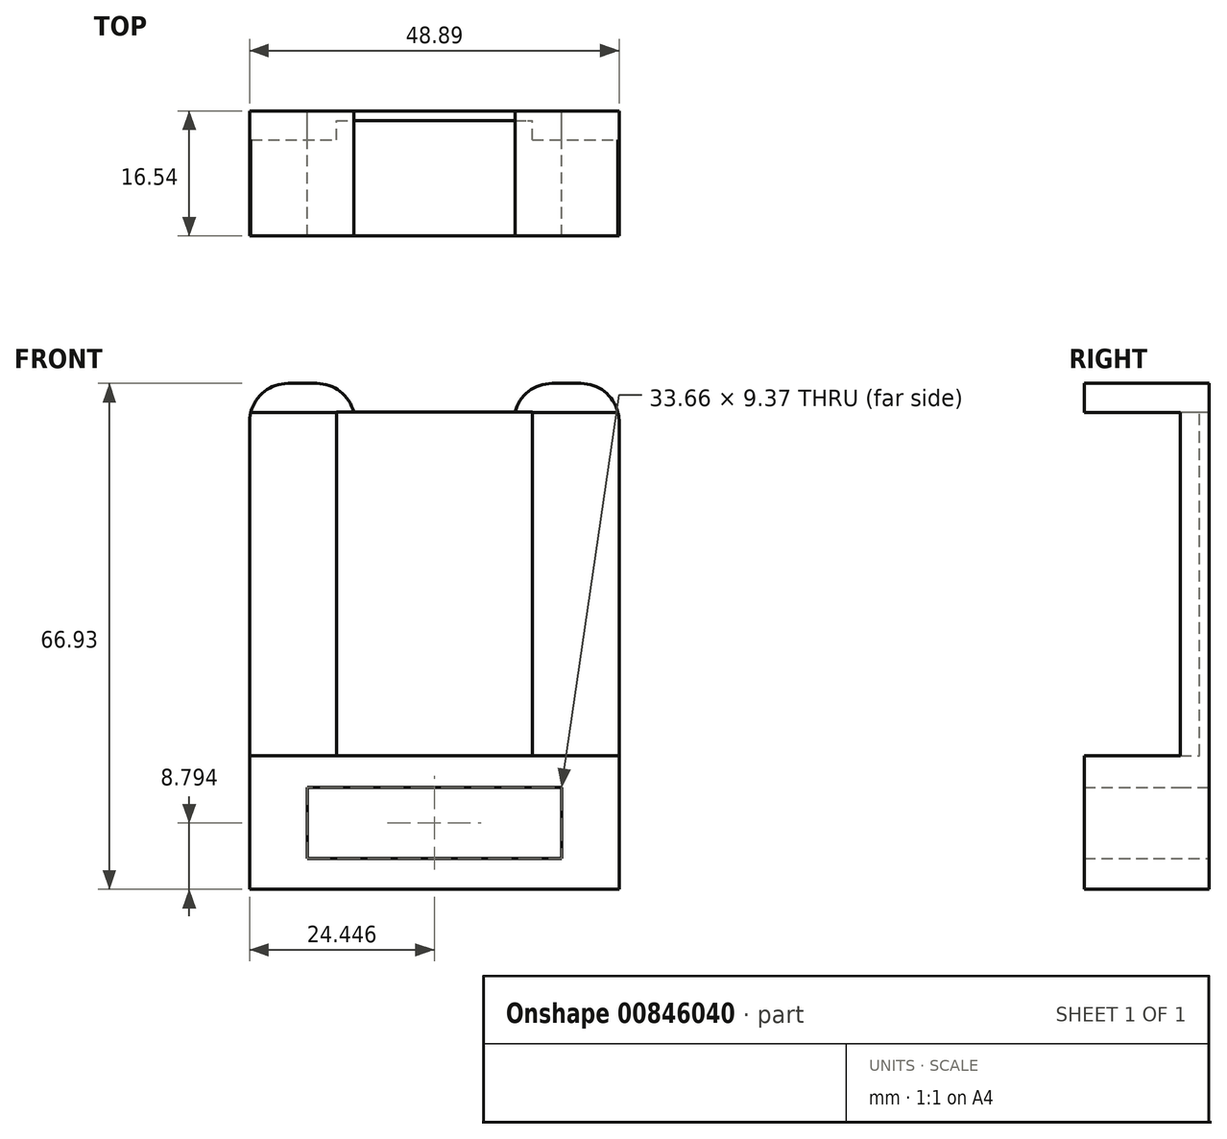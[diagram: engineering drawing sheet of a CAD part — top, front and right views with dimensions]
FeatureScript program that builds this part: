
annotation { "Feature Type Name" : "Feature", "Feature Type Description" : "" }
export const myFeature = defineFeature(function(context is Context, id is Id, definition is map)
    precondition{}
    {
        {
            var Q0;
            Q0=qCreatedBy(makeId("Front.planeOp"),FACE);
            var sketch = newSketch(context, id + "F0", { "sketchPlane" : qUnion([Q0])});
            skLineSegment(sketch, "E0.bottom", {"start": v(-13.58, -13.59) * mm, "end": v(20.07, -13.59) * mm});
            skLineSegment(sketch, "E0.top", {"start": v(-13.58, -4.22) * mm, "end": v(20.07, -4.22) * mm});
            skLineSegment(sketch, "E0.left", {"start": v(-13.58, -13.59) * mm, "end": v(-13.58, -4.22) * mm});
            skLineSegment(sketch, "E0.right", {"start": v(20.07, -13.59) * mm, "end": v(20.07, -4.22) * mm});
            skLineSegment(sketch, "E1.bottom", {"start": v(-21.2, -17.7) * mm, "end": v(27.7, -17.7) * mm});
            skLineSegment(sketch, "E1.left", {"start": v(-21.2, -17.7) * mm, "end": v(-21.2, 0) * mm});
            skLineSegment(sketch, "E1.right", {"start": v(27.7, -17.7) * mm, "end": v(27.7, 0) * mm});
            skLineSegment(sketch, "E2.bottom", {"start": v(-21.2, 0) * mm, "end": v(-9.7, 0) * mm});
            skLineSegment(sketch, "E2.top", {"start": v(-21.2, 45.42) * mm, "end": v(-9.7, 45.42) * mm});
            skLineSegment(sketch, "E2.left", {"start": v(-21.2, 0) * mm, "end": v(-21.2, 45.42) * mm});
            skLineSegment(sketch, "E2.right", {"start": v(-9.7, 0) * mm, "end": v(-9.7, 45.42) * mm});
            skPoint(sketch, "E3", {"position": v(3.25, 0) * mm});
            skLineSegment(sketch, "E4", {"start": v(3.25, 0) * mm, "end": v(3.25, 45.26) * mm, "construction": true});
            skLineSegment(sketch, "E5.MirrorCS", {"start": v(27.7, 45.42) * mm, "end": v(16.2, 45.42) * mm});
            skLineSegment(sketch, "E6.MirrorCS", {"start": v(27.7, 0) * mm, "end": v(27.7, 45.42) * mm});
            skLineSegment(sketch, "E7.MirrorCS", {"start": v(16.2, 0) * mm, "end": v(16.2, 45.42) * mm});
            skLineSegment(sketch, "E8", {"start": v(-9.7, 0) * mm, "end": v(-9.7, -4.22) * mm});
            skLineSegment(sketch, "E9", {"start": v(16.2, 0) * mm, "end": v(16.2, -4.22) * mm});
            skLineSegment(sketch, "E10", {"start": v(-9.7, 0) * mm, "end": v(16.2, 0) * mm});
            skLineSegment(sketch, "E11", {"start": v(16.2, 0) * mm, "end": v(27.7, 0) * mm});
            skLineSegment(sketch, "E12", {"start": v(-9.7, 45.42) * mm, "end": v(16.2, 45.42) * mm});
            skLineSegment(sketch, "E13.bottom", {"start": v(27.7, 45.42) * mm, "end": v(13.9, 45.42) * mm});
            skLineSegment(sketch, "E13.top", {"start": v(27.7, 49.23) * mm, "end": v(13.9, 49.23) * mm});
            skLineSegment(sketch, "E13.left", {"start": v(27.7, 45.42) * mm, "end": v(27.7, 49.23) * mm});
            skLineSegment(sketch, "E13.right", {"start": v(13.9, 45.42) * mm, "end": v(13.9, 49.23) * mm});
            skLineSegment(sketch, "E14.bottom", {"start": v(-21.2, 45.42) * mm, "end": v(-7.4, 45.42) * mm});
            skLineSegment(sketch, "E14.top", {"start": v(-21.2, 49.23) * mm, "end": v(-7.4, 49.23) * mm});
            skLineSegment(sketch, "E14.left", {"start": v(-21.2, 45.42) * mm, "end": v(-21.2, 49.23) * mm});
            skLineSegment(sketch, "E14.right", {"start": v(-7.4, 45.42) * mm, "end": v(-7.4, 49.23) * mm});
            skSolve(sketch);
        }
        {
            var Q0;
            Q0=makeQuery(id+"F0.imprint","IMPRINT",FACE,{"disambiguationData":[TD([[makeQuery(id+"F0.imprint","IMPRINT",EDGE,{"derivedFrom":sQuery(id+"F0.wireOp",EDGE,"E0.bottom")}),-1.0]])]});
            var Q1;
            {var subQ0=sQuery(id+"F0.wireOp",EDGE,"E6.MirrorCS");Q1=makeQuery(id+"F0.imprint","IMPRINT",FACE,{"disambiguationData":[TD([[makeQuery(id+"F0.imprint","IMPRINT",EDGE,{"derivedFrom":subQ0}),1.0]])]});}
            var Q2;
            Q2=makeQuery(id+"F0.imprint","IMPRINT",FACE,{"disambiguationData":[TD([[makeQuery(id+"F0.imprint","IMPRINT",EDGE,{"derivedFrom":sQuery(id+"F0.wireOp",EDGE,"E2.bottom")}),1.0]])]});
            var Q3;
            Q3=makeQuery(id+"F0.imprint","IMPRINT",FACE,{"disambiguationData":[TD([[makeQuery(id+"F0.imprint","IMPRINT",EDGE,{"derivedFrom":sQuery(id+"F0.wireOp",EDGE,"E13.top")}),1.0]])]});
            var Q4;
            Q4=makeQuery(id+"F0.imprint","IMPRINT",FACE,{"disambiguationData":[TD([[makeQuery(id+"F0.imprint","IMPRINT",EDGE,{"derivedFrom":sQuery(id+"F0.wireOp",EDGE,"E14.top")}),-1.0]])]});
            extrude(context, id + "F1", {"entities" : qUnion([Q0, Q1, Q2, Q3, Q4]), "depth" : 16.54 * mm, "offsetDistance" : 25.4 * mm});
        }
        {
            var Q0;
            {var subQ2=sQuery(id+"F0.wireOp",EDGE,"E2.right");Q0=makeQuery(id+"F0.imprint","IMPRINT",FACE,{"disambiguationData":[TD([[makeQuery(id+"F0.imprint","IMPRINT",EDGE,{"derivedFrom":subQ2}),-1.0]])]});}
            extrude(context, id + "F2", {"entities" : qUnion([Q0]), "operationType" : NewBodyOperationType.ADD, "depth" : 1.27 * mm, "offsetDistance" : 25.4 * mm});
        }
        {
            var Q0;
            {var subQ0=sQuery(id+"F0.wireOp",EDGE,"E8");Q0=makeQuery(id+"F0.imprint","IMPRINT",FACE,{"disambiguationData":[TD([[makeQuery(id+"F0.imprint","IMPRINT",EDGE,{"derivedFrom":subQ0}),1.0]])]});}
            extrude(context, id + "F3", {"entities" : qUnion([Q0]), "operationType" : NewBodyOperationType.ADD, "depth" : 7.62 * mm, "offsetDistance" : 25.4 * mm});
        }
        {
            var Q0;
            Q0=makeQuery(id+"F1.opExtrude","SWEPT_FACE",FACE,{"disambiguationData":[OSD([sQuery(id+"F0.wireOp",EDGE,"E1.left"),sQuery(id+"F0.wireOp",EDGE,"E2.left"),sQuery(id+"F0.wireOp",EDGE,"E14.left")])]});
            var sketch = newSketch(context, id + "F4", { "sketchPlane" : qUnion([Q0])});
            skLineSegment(sketch, "E15.bottom", {"start": v(3.84, -4.22) * mm, "end": v(16.54, -4.22) * mm});
            skLineSegment(sketch, "E15.top", {"start": v(3.84, 45.4) * mm, "end": v(16.54, 45.4) * mm});
            skLineSegment(sketch, "E15.left", {"start": v(3.84, -4.22) * mm, "end": v(3.84, 45.4) * mm});
            skLineSegment(sketch, "E15.right", {"start": v(16.54, -4.22) * mm, "end": v(16.54, 45.4) * mm});
            skSolve(sketch);
        }
        {
            var Q0;
            Q0=makeQuery(id+"F4.imprint","IMPRINT",FACE,{"disambiguationData":[TD([[makeQuery(id+"F4.imprint","IMPRINT",EDGE,{"derivedFrom":sQuery(id+"F4.wireOp",EDGE,"E15.bottom")}),1.0]])]});
            extrude(context, id + "F5", {"entities" : qUnion([Q0]), "operationType" : NewBodyOperationType.REMOVE, "oppositeDirection" : true, "depth" : 62.48 * mm, "offsetDistance" : 25.4 * mm});
        }
        {
            var Q0;
            Q0=makeQuery(id+"F1.opExtrude","SWEPT_EDGE",EDGE,{"disambiguationData":[OSD([sQuery(id+"F0.wireOp",EDGE,"E14.top"),sQuery(id+"F0.wireOp",EDGE,"E14.left")])]});
            var Q1;
            Q1=makeQuery(id+"F1.opExtrude","SWEPT_EDGE",EDGE,{"disambiguationData":[OSD([sQuery(id+"F0.wireOp",EDGE,"E14.top"),sQuery(id+"F0.wireOp",EDGE,"E14.right")])]});
            var Q2;
            Q2=makeQuery(id+"F1.opExtrude","SWEPT_EDGE",EDGE,{"disambiguationData":[OSD([sQuery(id+"F0.wireOp",EDGE,"E13.top"),sQuery(id+"F0.wireOp",EDGE,"E13.right")])]});
            var Q3;
            Q3=makeQuery(id+"F1.opExtrude","SWEPT_EDGE",EDGE,{"disambiguationData":[OSD([sQuery(id+"F0.wireOp",EDGE,"E13.top"),sQuery(id+"F0.wireOp",EDGE,"E13.left")])]});
            fillet(context, id + "F6", {"entities" : qUnion([Q0, Q1, Q2, Q3]), "radius" : 5.08 * mm, "tangentPropagation" : true, "allowEdgeOverflow" : false});
        }
        {
            var Q0;
            Q0=makeQuery(id+"F5.boolean.opBoolean","COPY",FACE,{"derivedFrom":makeQuery(id+"F5.opExtrude","SWEPT_FACE",FACE,{"disambiguationData":[OSD([sQuery(id+"F4.wireOp",EDGE,"E15.left")])]})});
            var sketch = newSketch(context, id + "F7", { "sketchPlane" : qUnion([Q0])});
            skLineSegment(sketch, "E16.bottom", {"start": v(-21.2, -4.22) * mm, "end": v(27.7, -4.22) * mm});
            skLineSegment(sketch, "E16.top", {"start": v(-21.2, 0) * mm, "end": v(27.7, 0) * mm});
            skLineSegment(sketch, "E16.left", {"start": v(-21.2, -4.22) * mm, "end": v(-21.2, 0) * mm});
            skLineSegment(sketch, "E16.right", {"start": v(27.7, -4.22) * mm, "end": v(27.7, 0) * mm});
            skSolve(sketch);
        }
        {
            var Q0;
            Q0 = qSketchRegion(id + "F7", true);
            var Q1;
            {var subQ0=sQuery(id+"F0.wireOp",EDGE,"E1.bottom");var subQ1=sQuery(id+"F0.wireOp",EDGE,"E0.right");var subQ2=sQuery(id+"F0.wireOp",EDGE,"E0.left");var subQ3=sQuery(id+"F0.wireOp",EDGE,"E0.bottom");var subQ4=sQuery(id+"F0.wireOp",EDGE,"E14.left");var subQ5=sQuery(id+"F0.wireOp",EDGE,"E2.left");var subQ6=sQuery(id+"F0.wireOp",EDGE,"E1.left");var subQ7=sQuery(id+"F0.wireOp",EDGE,"E13.left");var subQ8=sQuery(id+"F0.wireOp",EDGE,"E6.MirrorCS");var subQ9=sQuery(id+"F0.wireOp",EDGE,"E1.right");Q1=makeQuery(id+"F5.boolean.opBoolean","SPLIT",FACE,{"disambiguationData":[TD([makeQuery(id+"F1.opExtrude","SWEPT_FACE",FACE,{"disambiguationData":[OSD([subQ3])]})])],"derivedFrom":makeQuery(id+"F1.opExtrude","CAP_FACE",FACE,{"disambiguationData":[OSD([subQ3,sQuery(id+"F0.wireOp",EDGE,"E0.top"),subQ2,subQ1,subQ0,subQ6,subQ9,subQ5,sQuery(id+"F0.wireOp",EDGE,"E2.right"),subQ8,sQuery(id+"F0.wireOp",EDGE,"E7.MirrorCS"),sQuery(id+"F0.wireOp",EDGE,"E8"),sQuery(id+"F0.wireOp",EDGE,"E9"),sQuery(id+"F0.wireOp",EDGE,"E13.bottom"),sQuery(id+"F0.wireOp",EDGE,"E13.top"),subQ7,sQuery(id+"F0.wireOp",EDGE,"E13.right"),sQuery(id+"F0.wireOp",EDGE,"E14.bottom"),sQuery(id+"F0.wireOp",EDGE,"E14.top"),subQ4,sQuery(id+"F0.wireOp",EDGE,"E14.right")])],"isStart":false})});}
            extrude(context, id + "F8", {"entities" : qUnion([Q0]), "operationType" : NewBodyOperationType.ADD, "endBound" : BoundingType.UP_TO_SURFACE, "depth" : 12.62 * mm, "endBoundEntityFace" : qUnion([Q1]), "offsetDistance" : 25.4 * mm});
        }
    });
